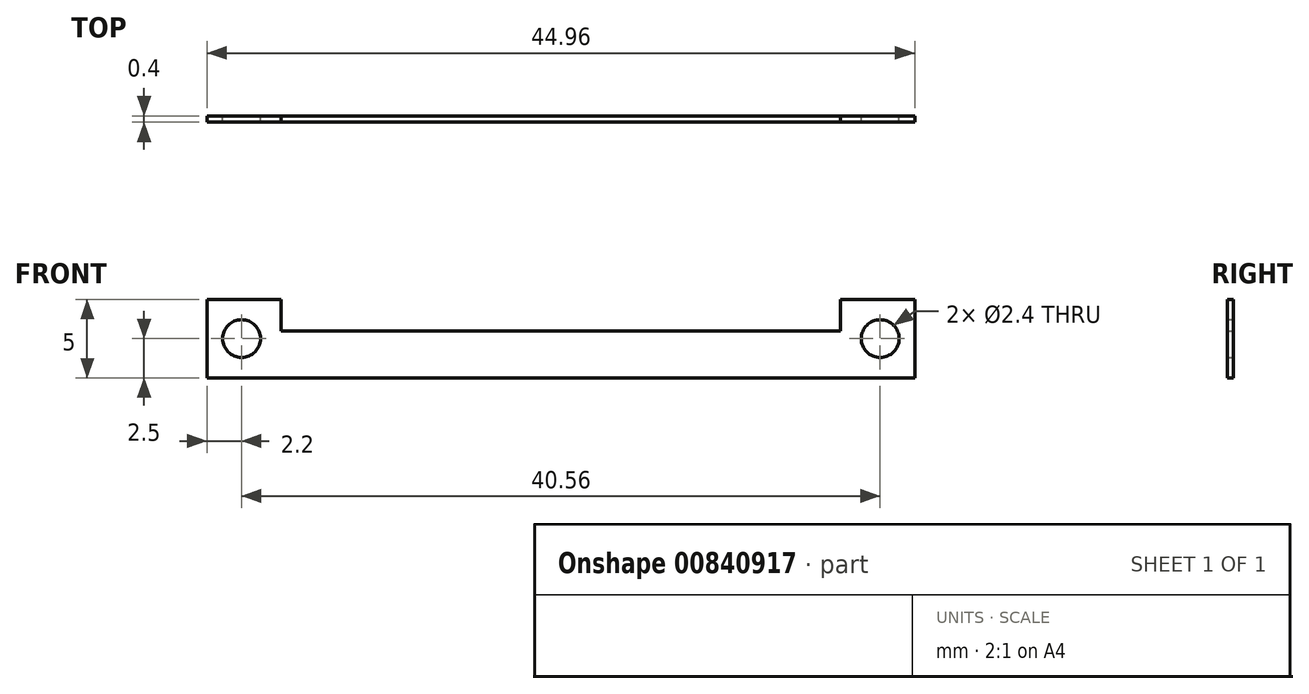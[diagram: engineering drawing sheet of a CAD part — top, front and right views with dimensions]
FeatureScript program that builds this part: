
annotation { "Feature Type Name" : "Feature", "Feature Type Description" : "" }
export const myFeature = defineFeature(function(context is Context, id is Id, definition is map)
    precondition{}
    {
        {
            var Q0;
            Q0=qCreatedBy(makeId("Front.planeOp"),FACE);
            var sketch = newSketch(context, id + "F0", { "sketchPlane" : qUnion([Q0])});
            skCircle(sketch, "E0", {"center": v(-20.28, 0) * mm, "radius": 1.2 * mm});
            skCircle(sketch, "E1", {"center": v(20.28, 0) * mm, "radius": 1.2 * mm});
            skLineSegment(sketch, "E2.bottom", {"start": v(-22.48, 2.5) * mm, "end": v(22.48, 2.5) * mm});
            skLineSegment(sketch, "E2.top", {"start": v(-22.48, -2.5) * mm, "end": v(22.48, -2.5) * mm});
            skLineSegment(sketch, "E2.left", {"start": v(-22.48, 2.5) * mm, "end": v(-22.48, -2.5) * mm});
            skLineSegment(sketch, "E2.right", {"start": v(22.48, 2.5) * mm, "end": v(22.48, -2.5) * mm});
            skLineSegment(sketch, "E3.bottom", {"start": v(-17.76, 2.5) * mm, "end": v(17.76, 2.5) * mm});
            skLineSegment(sketch, "E3.top", {"start": v(-17.76, 0.5) * mm, "end": v(17.76, 0.5) * mm});
            skLineSegment(sketch, "E3.left", {"start": v(-17.76, 2.5) * mm, "end": v(-17.76, 0.5) * mm});
            skLineSegment(sketch, "E3.right", {"start": v(17.76, 2.5) * mm, "end": v(17.76, 0.5) * mm});
            skSolve(sketch);
        }
        {
            var Q0;
            Q0=makeQuery(id+"F0.imprint","IMPRINT",FACE,{"disambiguationData":[TD([[makeQuery(id+"F0.imprint","IMPRINT",EDGE,{"derivedFrom":sQuery(id+"F0.wireOp",EDGE,"E0")}),-1.0]])]});
            extrude(context, id + "F1", {"entities" : qUnion([Q0]), "depth" : 0.4 * mm, "offsetDistance" : 25 * mm});
        }
    });
